# Revit family: 2120253 - Heavy Duty Toilet Roll Holder HDTX674
name_source: partatom
category: Specialty Equipment
units: mm (PartAtom-declared; Revit-internal decimal feet)

## family parameters
Always vertical = Yes
Cut with Voids When Loaded = No
OmniClass Number = 23.40.20.21.21
OmniClass Title = Toilet Paper Dispensers
Part Type = Normal
Room Calculation Point = No
Round Connector Dimension = Use Diameter
Shared = No
Work Plane-Based = No

## types (1)
- Heavy Duty Toilet Roll Holder HDTX674
    Assembly Code = C1030200
    Default Elevation = 0 mm  [stored 0 ft]
    Dimensions = 130mm x 415mm x 150mm
    Manufacturer = Franke South Africa (Pty) Ltd
    Material = Grade 304 18/10, satin finished
    Model = Heavy Duty Toilet Roll Holder HDTX674
    Product Code = 2120253

note: [stored X ft] marks values corroborated as IEEE doubles in the binary element streams (Revit-internal decimal feet)

## geometry (parser evidence)
native form markers: Sweep x3
no freeform markers — native parametric forms only
